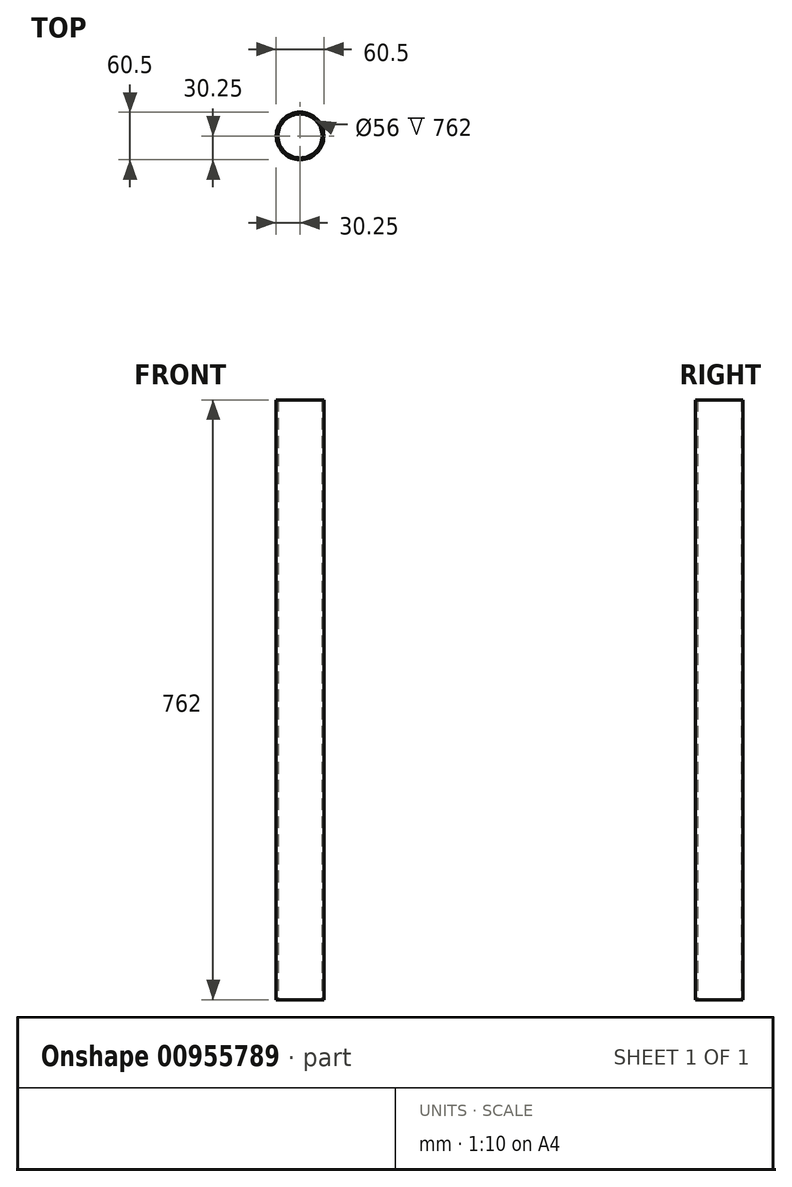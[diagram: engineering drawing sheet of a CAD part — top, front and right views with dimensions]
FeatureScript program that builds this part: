
annotation { "Feature Type Name" : "Feature", "Feature Type Description" : "" }
export const myFeature = defineFeature(function(context is Context, id is Id, definition is map)
    precondition{}
    {
        {
            var Q0;
            Q0=qCreatedBy(makeId("Top.planeOp"),FACE);
            var sketch = newSketch(context, id + "F0", { "sketchPlane" : qUnion([Q0])});
            skCircle(sketch, "E0", {"center": v(0, 0) * mm, "radius": 30.25 * mm});
            skCircle(sketch, "E1", {"center": v(0, 0) * mm, "radius": 28 * mm});
            skSolve(sketch);
        }
        {
            var Q0;
            Q0=makeQuery(id+"F0.imprint","IMPRINT",FACE,{"disambiguationData":[TD([[makeQuery(id+"F0.imprint","IMPRINT",EDGE,{"derivedFrom":sQuery(id+"F0.wireOp",EDGE,"E0")}),1.0]])]});
            extrude(context, id + "F1", {"entities" : qUnion([Q0]), "depth" : 762 * mm, "offsetDistance" : 25 * mm});
        }
    });
